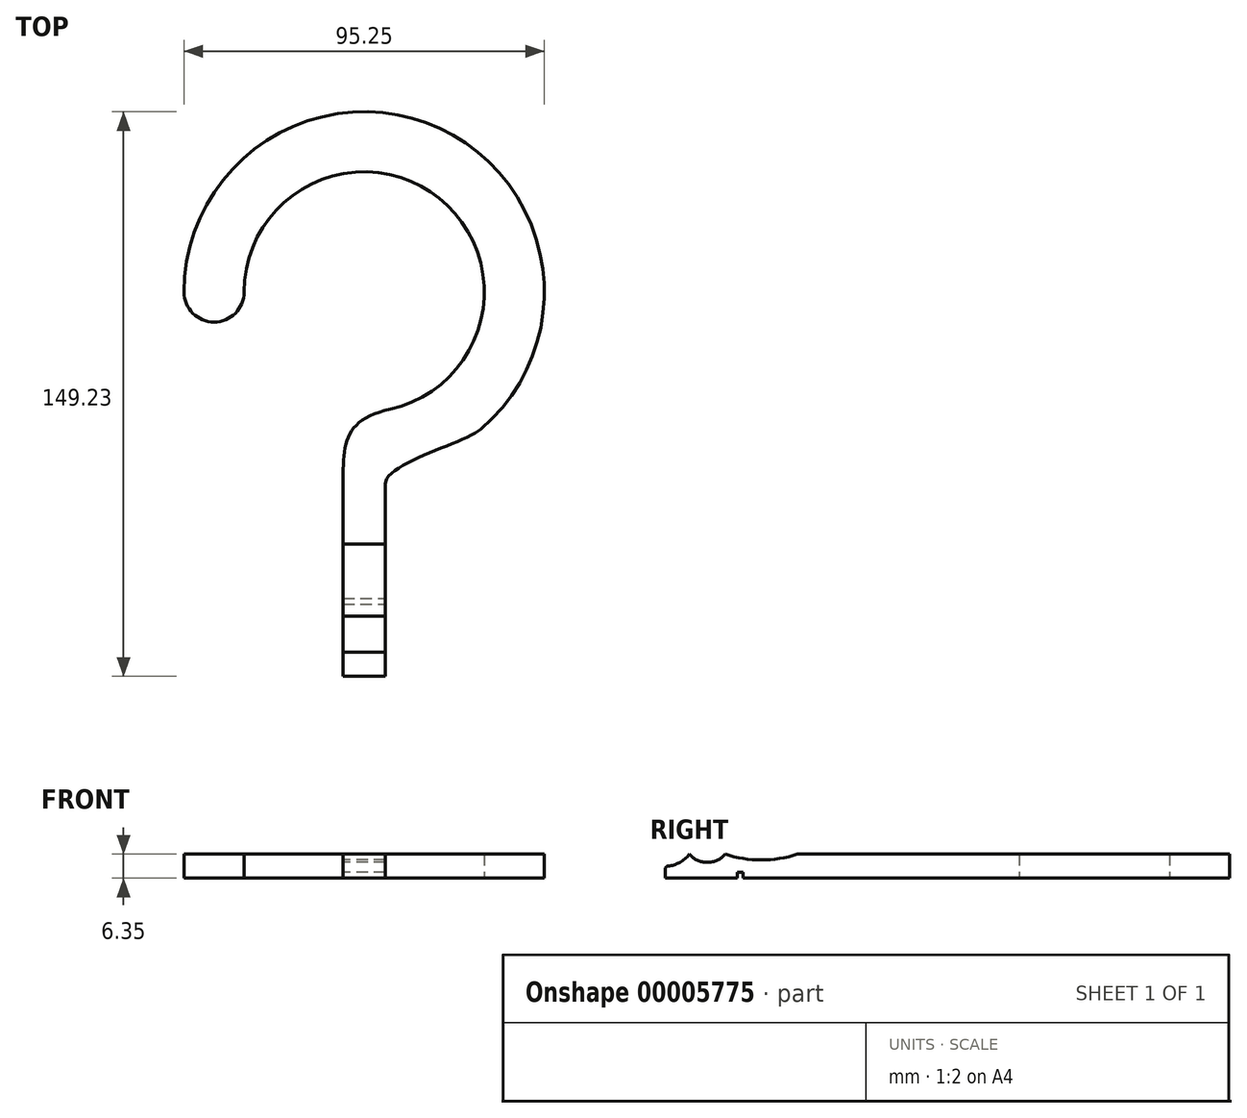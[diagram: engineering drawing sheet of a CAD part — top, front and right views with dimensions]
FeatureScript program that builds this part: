
annotation { "Feature Type Name" : "Feature", "Feature Type Description" : "" }
export const myFeature = defineFeature(function(context is Context, id is Id, definition is map)
    precondition{}
    {
        {
            var Q0;
            Q0=qCreatedBy(makeId("Top.planeOp"),FACE);
            var sketch = newSketch(context, id + "F0", { "sketchPlane" : qUnion([Q0])});
            skLineSegment(sketch, "E0", {"start": v(0, 0) * mm, "end": v(11.11, 0) * mm});
            skLineSegment(sketch, "E1", {"start": v(11.11, 0) * mm, "end": v(11.11, 50.8) * mm});
            skLineSegment(sketch, "E2", {"start": v(0, 0) * mm, "end": v(0, 50.8) * mm});
            skArc(sketch, "E3", {"start": v(12.5, 70.62) * mm, "mid": v(25.4, 126.38) * mm, "end": v(-26.2, 101.6) * mm});
            skArc(sketch, "E4", {"start": v(36.37, 65.29) * mm, "mid": v(25.57, 144.82) * mm, "end": v(-42.07, 101.6) * mm});
            skArc(sketch, "E5", {"start": v(-42.07, 101.6) * mm, "mid": v(-34.13, 93.66) * mm, "end": v(-26.2, 101.6) * mm});
            skFitSpline(sketch, "E6", {"points": [v(11.11, 50.8) * mm, v(36.37, 65.29) * mm], "startDerivative": vector(0, 17.03) * mm, "endDerivative": vector(13.3, 11.3) * mm});
            skFitSpline(sketch, "E7", {"points": [v(0, 50.8) * mm, v(12.5, 70.62) * mm], "startDerivative": vector(0, 31.97) * mm, "endDerivative": vector(37.48, 8.4) * mm});
            skPoint(sketch, "E8", {"position": v(5.56, 0) * mm});
            skLineSegment(sketch, "E9.bottom", {"start": v(53.18, 149.22) * mm, "end": v(-42.07, 149.22) * mm, "construction": true});
            skLineSegment(sketch, "E9.top", {"start": v(53.18, 0) * mm, "end": v(-42.07, 0) * mm, "construction": true});
            skLineSegment(sketch, "E9.left", {"start": v(53.18, 149.22) * mm, "end": v(53.18, 0) * mm, "construction": true});
            skLineSegment(sketch, "E9.right", {"start": v(-42.07, 149.22) * mm, "end": v(-42.07, 0) * mm, "construction": true});
            skPoint(sketch, "E9.middle", {"position": v(5.56, 74.61) * mm});
            skSolve(sketch);
        }
        {
            var Q0;
            Q0=makeQuery(id+"F0.imprint","IMPRINT",FACE,{"disambiguationData":[TD([[makeQuery(id+"F0.imprint","IMPRINT",EDGE,{"derivedFrom":sQuery(id+"F0.wireOp",EDGE,"E3")}),-1.0]])]});
            extrude(context, id + "F1", {"entities" : qUnion([Q0]), "depth" : 6.35 * mm});
        }
        {
            var Q0;
            Q0=qCreatedBy(makeId("Right.planeOp"),FACE);
            var sketch = newSketch(context, id + "F2", { "sketchPlane" : qUnion([Q0])});
            skCircle(sketch, "E10", {"center": v(11.11, 10.55) * mm, "radius": 6.35 * mm});
            skPoint(sketch, "E11", {"position": v(15.88, 6.35) * mm});
            skPoint(sketch, "E12", {"position": v(6.35, 6.35) * mm});
            skCircle(sketch, "E13", {"center": v(25.4, 35.35) * mm, "radius": 30.53 * mm});
            skPoint(sketch, "E14", {"position": v(34.92, 6.35) * mm});
            skPoint(sketch, "E15", {"position": v(25.4, 4.83) * mm});
            skCircle(sketch, "E16", {"center": v(38.23, 6.35) * mm, "radius": 3.3 * mm});
            skCircle(sketch, "E17", {"center": v(0, 11.11) * mm, "radius": 7.94 * mm});
            skPoint(sketch, "E18", {"position": v(0, 3.18) * mm});
            skLineSegment(sketch, "E19.bottom", {"start": v(19.05, -1.59) * mm, "end": v(20.64, -1.59) * mm});
            skLineSegment(sketch, "E19.top", {"start": v(19.05, 1.59) * mm, "end": v(20.64, 1.59) * mm});
            skLineSegment(sketch, "E19.left", {"start": v(19.05, -1.59) * mm, "end": v(19.05, 1.59) * mm});
            skLineSegment(sketch, "E19.right", {"start": v(20.64, -1.59) * mm, "end": v(20.64, 1.59) * mm});
            skPoint(sketch, "E19.middle", {"position": v(19.84, 0) * mm});
            skSolve(sketch);
        }
        {
            var Q0;
            {var subQ0=sQuery(id+"F2.wireOp",EDGE,"E16");var subQ1=sQuery(id+"F2.wireOp",EDGE,"E13");var subQ2=makeQuery(id+"F2.imprint","INTERSECT",VERTEX,{"disambiguationData":[OD(0.0)],"derivedFrom":[subQ1,subQ0]});Q0=makeQuery(id+"F2.imprint","IMPRINT",FACE,{"disambiguationData":[TD([[makeQuery(id+"F2.imprint","IMPRINT",EDGE,{"disambiguationData":[TD([[subQ2,-1.0]])],"derivedFrom":subQ1}),-1.0]])]});}
            var Q1;
            {var subQ0=sQuery(id+"F2.wireOp",EDGE,"E13");var subQ1=sQuery(id+"F2.wireOp",EDGE,"E10");var subQ2=makeQuery(id+"F2.imprint","INTERSECT",VERTEX,{"disambiguationData":[OD(0.0)],"derivedFrom":[subQ1,subQ0]});Q1=makeQuery(id+"F2.imprint","IMPRINT",FACE,{"disambiguationData":[TD([[makeQuery(id+"F2.imprint","IMPRINT",EDGE,{"disambiguationData":[TD([[subQ2,-1.0]])],"derivedFrom":subQ1}),-1.0]])]});}
            var Q2;
            {var subQ0=sQuery(id+"F2.wireOp",EDGE,"E13");var subQ1=sQuery(id+"F2.wireOp",EDGE,"E10");var subQ2=makeQuery(id+"F2.imprint","INTERSECT",VERTEX,{"disambiguationData":[OD(0.0)],"derivedFrom":[subQ1,subQ0]});Q2=makeQuery(id+"F2.imprint","IMPRINT",FACE,{"disambiguationData":[TD([[makeQuery(id+"F2.imprint","IMPRINT",EDGE,{"disambiguationData":[TD([[subQ2,1.0]])],"derivedFrom":subQ1}),1.0]])]});}
            var Q3;
            {var subQ0=sQuery(id+"F2.wireOp",EDGE,"E17");var subQ1=sQuery(id+"F2.wireOp",EDGE,"E10");var subQ2=makeQuery(id+"F2.imprint","INTERSECT",VERTEX,{"disambiguationData":[OD(0.0)],"derivedFrom":[subQ1,subQ0]});Q3=makeQuery(id+"F2.imprint","IMPRINT",FACE,{"disambiguationData":[TD([[makeQuery(id+"F2.imprint","IMPRINT",EDGE,{"disambiguationData":[TD([[subQ2,1.0]])],"derivedFrom":subQ1}),-1.0]])]});}
            var Q4;
            Q4=makeQuery(id+"F2.imprint","IMPRINT",FACE,{"disambiguationData":[TD([[makeQuery(id+"F2.imprint","IMPRINT",EDGE,{"derivedFrom":sQuery(id+"F2.wireOp",EDGE,"E19.bottom")}),1.0]])]});
            extrude(context, id + "F3", {"entities" : qUnion([Q0, Q1, Q2, Q3, Q4]), "operationType" : NewBodyOperationType.REMOVE, "depth" : 25.4 * mm});
        }
        {
            var Q0;
            {var subQ0=sQuery(id+"F2.wireOp",EDGE,"E17");var subQ1=sQuery(id+"F2.wireOp",EDGE,"E10");var subQ2=makeQuery(id+"F2.imprint","INTERSECT",VERTEX,{"disambiguationData":[OD(0.0)],"derivedFrom":[subQ1,subQ0]});var subQ3=sQuery(id+"F2.wireOp",EDGE,"E13");var subQ5=makeQuery(id+"F2.imprint","INTERSECT",VERTEX,{"disambiguationData":[OD(0.0)],"derivedFrom":[subQ1,subQ3]});var subQ6=makeQuery(id+"F2.imprint","INTERSECT",VERTEX,{"disambiguationData":[OD(0.0)],"derivedFrom":[subQ3,subQ0]});Q0=makeQuery(id+"F3.boolean.opBoolean","TWEAK_EDGE",EDGE,{"derivedFrom":[makeQuery(id+"F3.opExtrude","SWEPT_EDGE",EDGE,{"disambiguationData":[OSD([subQ1,subQ0]),TDD([subQ2]),ownerDisambiguation([makeQuery(id+"F3.opExtrude","SWEPT_BODY",BODY,{"disambiguationData":[OSD([subQ1,subQ3,subQ0]),TDD([makeQuery(id+"F2.imprint","IMPRINT",EDGE,{"disambiguationData":[TD([[subQ2,1.0]])],"derivedFrom":subQ1}),makeQuery(id+"F2.imprint","IMPRINT",EDGE,{"disambiguationData":[TD([[subQ6,-1.0]])],"derivedFrom":subQ3}),makeQuery(id+"F2.imprint","IMPRINT",EDGE,{"disambiguationData":[TD([[subQ2,1.0]])],"derivedFrom":subQ0})])]})])]}),makeQuery(id+"F3.opExtrude","SWEPT_EDGE",EDGE,{"disambiguationData":[OSD([subQ1,subQ0]),TDD([subQ2]),ownerDisambiguation([makeQuery(id+"F3.opExtrude","SWEPT_BODY",BODY,{"disambiguationData":[OSD([subQ1,subQ3,subQ0]),TDD([makeQuery(id+"F2.imprint","IMPRINT",EDGE,{"disambiguationData":[TD([[subQ2,-1.0]])],"derivedFrom":subQ1}),makeQuery(id+"F2.imprint","IMPRINT",EDGE,{"disambiguationData":[TD([[subQ5,1.0]])],"derivedFrom":subQ3}),makeQuery(id+"F2.imprint","IMPRINT",EDGE,{"disambiguationData":[TD([[subQ2,-1.0]])],"derivedFrom":subQ0})])]})])]})]});}
            var Q1;
            {var subQ0=sQuery(id+"F2.wireOp",EDGE,"E17");var subQ1=sQuery(id+"F2.wireOp",EDGE,"E13");var subQ2=sQuery(id+"F2.wireOp",EDGE,"E10");var subQ3=makeQuery(id+"F2.imprint","INTERSECT",VERTEX,{"disambiguationData":[OD(0.0)],"derivedFrom":[subQ2,subQ1]});var subQ4=makeQuery(id+"F2.imprint","INTERSECT",VERTEX,{"disambiguationData":[OD(0.0)],"derivedFrom":[subQ2,subQ0]});Q1=makeQuery(id+"F3.boolean.opBoolean","TWEAK_EDGE",EDGE,{"derivedFrom":[makeQuery(id+"F3.opExtrude","SWEPT_EDGE",EDGE,{"disambiguationData":[OSD([subQ2,subQ1]),TDD([subQ3]),ownerDisambiguation([makeQuery(id+"F3.opExtrude","SWEPT_BODY",BODY,{"disambiguationData":[OSD([subQ2,subQ1,subQ0]),TDD([makeQuery(id+"F2.imprint","IMPRINT",EDGE,{"disambiguationData":[TD([[subQ4,-1.0]])],"derivedFrom":subQ2}),makeQuery(id+"F2.imprint","IMPRINT",EDGE,{"disambiguationData":[TD([[subQ3,1.0]])],"derivedFrom":subQ1}),makeQuery(id+"F2.imprint","IMPRINT",EDGE,{"disambiguationData":[TD([[subQ4,-1.0]])],"derivedFrom":subQ0})])]})])]}),makeQuery(id+"F3.opExtrude","SWEPT_EDGE",EDGE,{"disambiguationData":[OSD([subQ2,subQ1]),TDD([subQ3]),ownerDisambiguation([makeQuery(id+"F3.opExtrude","SWEPT_BODY",BODY,{"disambiguationData":[OSD([subQ2,subQ1,sQuery(id+"F2.wireOp",EDGE,"E16"),subQ0])]})])]})]});}
            var Q2;
            {var subQ0=sQuery(id+"F2.wireOp",EDGE,"E16");var subQ1=sQuery(id+"F2.wireOp",EDGE,"E13");var subQ2=makeQuery(id+"F2.imprint","INTERSECT",VERTEX,{"disambiguationData":[OD(0.0)],"derivedFrom":[subQ1,subQ0]});Q2=makeQuery(id+"F3.boolean.opBoolean","TWEAK_EDGE",EDGE,{"derivedFrom":[makeQuery(id+"F3.opExtrude","SWEPT_EDGE",EDGE,{"disambiguationData":[OSD([subQ1,subQ0]),TDD([subQ2]),ownerDisambiguation([makeQuery(id+"F3.opExtrude","SWEPT_BODY",BODY,{"disambiguationData":[OSD([sQuery(id+"F2.wireOp",EDGE,"E10"),subQ1,subQ0,sQuery(id+"F2.wireOp",EDGE,"E17")])]})])]}),makeQuery(id+"F3.opExtrude","SWEPT_EDGE",EDGE,{"disambiguationData":[OSD([subQ1,subQ0]),TDD([subQ2]),ownerDisambiguation([makeQuery(id+"F3.opExtrude","SWEPT_BODY",BODY,{"disambiguationData":[OSD([subQ1,subQ0])]})])]})]});}
            var Q3;
            {var subQ0=sQuery(id+"F2.wireOp",EDGE,"E16");var subQ1=sQuery(id+"F2.wireOp",EDGE,"E13");Q3=makeQuery(id+"F3.boolean.opBoolean","INTERSECT",EDGE,{"derivedFrom":[makeQuery(id+"F1.opExtrude","CAP_FACE",FACE,{"disambiguationData":[OSD([sQuery(id+"F0.wireOp",EDGE,"E0"),sQuery(id+"F0.wireOp",EDGE,"E1"),sQuery(id+"F0.wireOp",EDGE,"E2"),sQuery(id+"F0.wireOp",EDGE,"E3"),sQuery(id+"F0.wireOp",EDGE,"E4"),sQuery(id+"F0.wireOp",EDGE,"E5"),sQuery(id+"F0.wireOp",EDGE,"E6"),sQuery(id+"F0.wireOp",EDGE,"E7")])],"isStart":false}),makeQuery(id+"F3.opExtrude","SWEPT_FACE",FACE,{"disambiguationData":[OSD([subQ0]),TDD([makeQuery(id+"F2.imprint","IMPRINT",EDGE,{"disambiguationData":[TD([[makeQuery(id+"F2.imprint","INTERSECT",VERTEX,{"disambiguationData":[OD(0.0)],"derivedFrom":[subQ1,subQ0]}),-1.0]])],"derivedFrom":subQ0})])]})]});}
            var Q4;
            {var subQ0=sQuery(id+"F2.wireOp",EDGE,"E17");Q4=makeQuery(id+"F3.boolean.opBoolean","INTERSECT",EDGE,{"derivedFrom":[makeQuery(id+"F1.opExtrude","SWEPT_FACE",FACE,{"disambiguationData":[OSD([sQuery(id+"F0.wireOp",EDGE,"E0")])]}),makeQuery(id+"F3.opExtrude","SWEPT_FACE",FACE,{"disambiguationData":[OSD([subQ0]),TDD([makeQuery(id+"F2.imprint","IMPRINT",EDGE,{"disambiguationData":[TD([[makeQuery(id+"F2.imprint","INTERSECT",VERTEX,{"disambiguationData":[OD(0.0)],"derivedFrom":[sQuery(id+"F2.wireOp",EDGE,"E10"),subQ0]}),1.0]])],"derivedFrom":subQ0})])]})]});}
            fillet(context, id + "F4", {"entities" : qUnion([Q0, Q1, Q2, Q3, Q4]), "radius" : 0.76 * mm, "tangentPropagation" : true, "allowEdgeOverflow" : false});
        }
        {
            var Q0;
            Q0=qCreatedBy(makeId("Top.planeOp"),FACE);
            var sketch = newSketch(context, id + "F5", { "sketchPlane" : qUnion([Q0])});
            skLineSegment(sketch, "E20", {"start": v(2.38, 42.03) * mm, "end": v(4.38, 34.07) * mm});
            skLineSegment(sketch, "E21", {"start": v(4.38, 34.07) * mm, "end": v(5.15, 34.26) * mm});
            skLineSegment(sketch, "E22", {"start": v(5.15, 34.26) * mm, "end": v(3.15, 42.22) * mm});
            skLineSegment(sketch, "E23", {"start": v(3.15, 42.22) * mm, "end": v(2.38, 42.03) * mm});
            skLineSegment(sketch, "E24.0", {"start": v(0, 42.22) * mm, "end": v(11.11, 42.22) * mm, "construction": true});
            skLineSegment(sketch, "E25.0", {"start": v(11.11, 34.07) * mm, "end": v(0, 34.07) * mm, "construction": true});
            skPoint(sketch, "E26", {"position": v(2.77, 34.07) * mm});
            skPoint(sketch, "E26.positionSnap0", {"position": v(2.77, 42.12) * mm});
            skSolve(sketch);
        }
        {
            var Q0;
            Q0=makeQuery(id+"F5.imprint","IMPRINT",FACE,{"disambiguationData":[TD([[makeQuery(id+"F5.imprint","IMPRINT",EDGE,{"derivedFrom":sQuery(id+"F5.wireOp",EDGE,"E20")}),1.0]])]});
            extrude(context, id + "F6", {"entities" : qUnion([Q0]), "operationType" : NewBodyOperationType.ADD, "depth" : 5.97 * mm});
        }
    });
